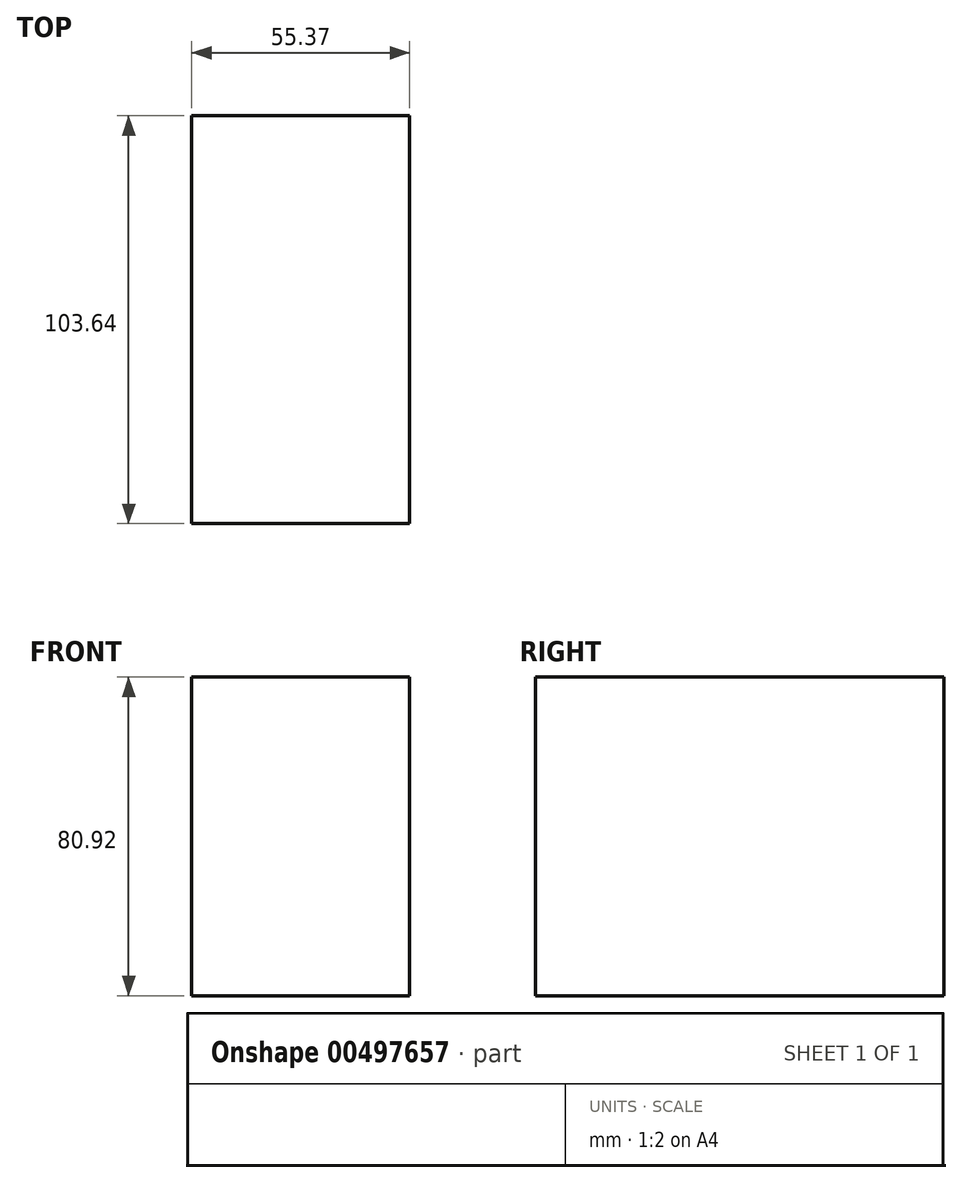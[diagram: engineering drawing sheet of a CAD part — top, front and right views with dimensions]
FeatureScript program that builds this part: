
annotation { "Feature Type Name" : "Feature", "Feature Type Description" : "" }
export const myFeature = defineFeature(function(context is Context, id is Id, definition is map)
    precondition{}
    {
        {
            var Q0;
            Q0=qCreatedBy(makeId("Right.planeOp"),FACE);
            var sketch = newSketch(context, id + "F0", { "sketchPlane" : qUnion([Q0])});
            skLineSegment(sketch, "E0.bottom", {"start": v(-51.82, 40.46) * mm, "end": v(51.82, 40.46) * mm});
            skLineSegment(sketch, "E0.top", {"start": v(-51.82, -40.46) * mm, "end": v(51.82, -40.46) * mm});
            skLineSegment(sketch, "E0.left", {"start": v(-51.82, 40.46) * mm, "end": v(-51.82, -40.46) * mm});
            skLineSegment(sketch, "E0.right", {"start": v(51.82, 40.46) * mm, "end": v(51.82, -40.46) * mm});
            skPoint(sketch, "E0.middle", {"position": v(0, 0) * mm});
            skSolve(sketch);
        }
        {
            var Q0;
            Q0=makeQuery(id+"F0.imprint","IMPRINT",FACE,{"disambiguationData":[TD([[makeQuery(id+"F0.imprint","IMPRINT",EDGE,{"derivedFrom":sQuery(id+"F0.wireOp",EDGE,"E0.bottom")}),-1.0]])]});
            extrude(context, id + "F1", {"entities" : qUnion([Q0]), "depth" : 55.37 * mm});
        }
    });
